# Revit family: EKF_EE_БоковыеСтенкиFORT_IP54_PROxima
name_source: partatom
category: Электрооборудование
units: mm (PartAtom-declared; Revit-internal decimal feet)

## family parameters
Всегда вертикально = Нет
На основе рабочей плоскости = Да
Общий = Да
При загрузке вырезать с полостями = Нет
Размер круглого соединителя = Использовать диаметр
Тип детали = Силовой щит
Точка расчета площади = Нет

## types (9) — shared parameters
ADSK_Единица измерения = шт.
ADSK_Завод-изготовитель = EKF
ADSK_Количество = 1
ADSK_Марка = Боковые стенки FORT
ADSK_Материал = RAL 7035_Сталь
ADSK_Обозначение = Боковые стенки FORT
ADSK_Размер_Глубина = 17.5 мм
Изготовитель = EKF
Серия номенклатуры = PROxima
Степень защиты IP = IP54
ТВ = EKF_2
Тип установки = -
zero-valued in all types: ADSK_Масса, Отметка по умолчанию

## per-type parameters (varying)
| type | ADSK_Код изделия | ADSK_Размер_Высота | ADSK_Размер_Ширина | Тип |
| Боковые стенки FORT IP54 для корпуса высотой 1800 и глубиной 400 (2шт.) EKF PROxima | FB184G | 1800 мм | 400 мм | 207 мм |
| Боковые стенки FORT IP54 для корпуса высотой 1800 и глубиной 600 (2шт.) EKF PROxima | FB186G | 1800 мм | 600 мм | 208 мм |
| Боковые стенки FORT IP54 для корпуса высотой 1800 и глубиной 800 (2шт.) EKF PROxima | FB188G | 1800 мм | 800 мм | 209 мм |
| Боковые стенки FORT IP54 для корпуса высотой 2000 и глубиной 400 (2шт.) EKF PROxima | FB204G | 2000 мм | 400 мм | 210 мм |
| Боковые стенки FORT IP54 для корпуса высотой 2000 и глубиной 600 (2шт.) EKF PROxima | FB206G | 2000 мм | 600 мм | 211 мм |
| Боковые стенки FORT IP54 для корпуса высотой 2000 и глубиной 800 (2шт.) EKF PROxima | FB208G | 2000 мм | 800 мм | 212 мм |
| Боковые стенки FORT IP54 для корпуса высотой 2200 и глубиной 400 (2шт.) EKF PROxima | FB224G | 2200 мм | 400 мм | 213 мм |
| Боковые стенки FORT IP54 для корпуса высотой 2200 и глубиной 600 (2шт.) EKF PROxima | FB226G | 2200 мм | 600 мм | 214 мм |
| Боковые стенки FORT IP54 для корпуса высотой 2200 и глубиной 800 (2шт.) EKF PROxima | FB228G | 2200 мм | 800 мм | 215 мм |

note: column(s) folded — value = type name in every type: ADSK_Наименование
